# Revit family: QF_MACON_CB92C-G-N
name_source: partatom
category: Specialty Equipment
units: mm (PartAtom-declared; Revit-internal decimal feet)

## family parameters
Always vertical = Yes
Cut with Voids When Loaded = No
OmniClass Number = 23.40.40.14.17.11
OmniClass Title = Cookers, Ovens, Stoves
Part Type = Normal
Room Calculation Point = No
Round Connector Dimension = Use Diameter
Shared = No
Work Plane-Based = No

## types (2) — shared parameters
Depth = 972,00 mm
Gas Connection Height = 62,00 mm
Gas Pressure = 0,0 bar
Gas Size = 1"
Height = 351,00 mm
Manufacturer = MACOM
Show Clearances = Yes
URL = https://www.acosmacom.com.br
Volume = 0,29 m³
Weight = 0,00 kg
Width = 900,00 mm

## per-type parameters (varying)
| type | Description | Gas Consumption GLP | Gas Consumption GN | Gas Input GLP | Gas Input GN |
| CB92C-G | CHAR BROILER A GAS GLP 900HP MACOM - 900X972X265MM | 2,06 Kg/h | 0,0 m³/h | 93700 Btu/h |  |
| CB92C-N | CHAR BROILER A GAS NATURAL 900HP MACOM - 900X972X265MM-900X972X265 |  | 2,5 m³/h | 0 Btu/h | 23600 Kcal/h |

note: column(s) folded — value = type name in every type: Model

## geometry (parser evidence)
native form markers: Sweep x6
no freeform markers — native parametric forms only
